# Revit family: Hager-UNIVERS-Hollow_wall-IP30-With_Cover-With_DIN-Hosted-DE-de
name_source: partatom
category: Electrical Equipment
units: mm (PartAtom-declared; Revit-internal decimal feet)

## family parameters
Cut with Voids When Loaded = No
Host = Face
Maintain Annotation Orientation = Yes
Panel Configuration = Two Columns, Circuits Across
Part Type = Panelboard
Room Calculation Point = No
Round Connector Dimension = Use Diameter
Shared = No

## types (28) — shared parameters
BC_MODEL_ID = 1539180
BC_OBJECT_ID = 512281
BC_OBJECT_VERSION = #6
Code hager = ADD-EC000214_EU
EF000003 - Montageart = Hohlwand
EF000007 - Farbe = weiß
EF000024 - UV-beständig = No
EF000049 - Tiefe = 125 mm  [stored 0.410105 ft]
EF000116 - RAL-Nummer = 9010
EF000118 - Mit Montageplatte = No
EF000218 - Einbautiefe = 112 mm  [stored 0.367454 ft]
EF001062 - EMV-Ausführung = No
EF001088 - Anbaumöglichkeit = Yes
EF001134 - DIN-Schiene = Yes
EF002950 - Breite in Teilungseinheiten = 12
EF004462 - Art der Schließung = sonstige
EF005474 - Schutzart (IP) = IP30
EF006244 - Transparenter Deckel/Tür = No
EF006306 - Mit Schloss = No
EF015941 - Signaldurchlassende Tür = No
ETIM class code = EC000214
ETIM class name = Small distribution board
HG000002-Mit tür = Yes
HG000003-Bereich = UNIVERS
HG000005-Dicke = 2 mm  [stored 0.00656168 ft]
HG000006-Flush mounted = Yes
HG000011-Leere Reihen von unten = No
HG000012-Türschwenkwinkel = 90.00°
HG000013-Tür links = No
HG000014-Tür rechts = Yes
HG000015-Sichtbarkeit der Türöffnung = Yes
HG000016-3D-Türsichtbarkeit = Yes
HG000017-Distanz zwischen den Polen = 18 mm  [stored 0.0590551 ft]
HG000060-RAL-number = 9010
HG000099-Onfly Template ID-de-DE = 507532
HGEF0002950-Breite in Teilungseinheiten = 12
Manufacturer = Hager
Name = Hager-UNIVERS-Hollow_wall-IP30-With_Cover-With_DIN-NoHosted-DE-de
Name BIM&CO = Electricity
Name hager = ADD_Enclosures_EC000214
Uniformat = Low Tension Service & Dist.
Uniformat code = D501001
zero-valued in all types: Default Elevation, EF001131 - Innentiefe, HG000007-Anzahl der leeren Spalten, HG000008-Anzahl der leeren Reihen

## per-type parameters (varying)
| type | BC_VARIANT_ID | EF000008 - Breite | EF000040 - Höhe | EF000266 - Anzahl der Reihen | EF000332 - Einbauhöhe | EF000846 - Einbaubreite | EF009212 - Ausführung Deckel | EF015776 - Erdungsklemmenblock | EF015777 - Neutralleiterklemmenblock | HG000001-Anzahl der Spalten | HG000004-Herstellerreferenz | HG000009-Doppelflügeligen Tür | HG000010-Asymmetrische Türen | HGEF000266-Anzahl der Reihen |
| UNIVERS-Hollow_wall_W353_H553_D125_12_Modular_Spacing-FWU31A | 1169890 | 353 mm  [stored 1.15814 ft] | 553 mm  [stored 1.8143 ft] | 3 | 502 mm  [stored 1.64698 ft] | 310 mm  [stored 1.01706 ft] | geschlossen | No | No | 1 | FWU31A | No | No | 3 |
| UNIVERS-Hollow_wall_W353_H553_D125_12_Modular_Spacing-FWU31S | 1169891 | 353 mm  [stored 1.15814 ft] | 553 mm  [stored 1.8143 ft] | 3 | 502 mm  [stored 1.64698 ft] | 310 mm  [stored 1.01706 ft] | mit Ausschnitt | Yes | Yes | 1 | FWU31S | No | No | 3 |
| UNIVERS-Hollow_wall_W603_H553_D125_12_Modular_Spacing-FWU32A | 1169892 | 603 mm | 553 mm  [stored 1.8143 ft] | 3 | 502 mm  [stored 1.64698 ft] | 560 mm  [stored 1.83727 ft] | geschlossen | No | No | 2 | FWU32A | No | No | 3 |
| UNIVERS-Hollow_wall_W603_H553_D125_12_Modular_Spacing-FWU32S | 1169893 | 603 mm | 553 mm  [stored 1.8143 ft] | 3 | 502 mm  [stored 1.64698 ft] | 560 mm  [stored 1.83727 ft] | mit Ausschnitt | Yes | No | 2 | FWU32S | No | No | 3 |
| UNIVERS-Hollow_wall_W853_H553_D125_12_Modular_Spacing-FWU33A | 1169894 | 853 mm  [stored 2.79856 ft] | 553 mm  [stored 1.8143 ft] | 3 | 502 mm  [stored 1.64698 ft] | 810 mm | geschlossen | No | No | 3 | FWU33A | Yes | Yes | 3 |
| UNIVERS-Hollow_wall_W853_H553_D125_12_Modular_Spacing-FWU33S | 1169895 | 853 mm  [stored 2.79856 ft] | 553 mm  [stored 1.8143 ft] | 3 | 502 mm  [stored 1.64698 ft] | 810 mm | mit Ausschnitt | Yes | No | 3 | FWU33S | Yes | Yes | 3 |
| UNIVERS-Hollow_wall_W353_H703_D125_12_Modular_Spacing-FWU41A | 1169896 | 353 mm  [stored 1.15814 ft] | 703 mm  [stored 2.30643 ft] | 4 | 652 mm  [stored 2.13911 ft] | 310 mm  [stored 1.01706 ft] | geschlossen | No | No | 1 | FWU41A | No | No | 4 |
| UNIVERS-Hollow_wall_W353_H703_D125_12_Modular_Spacing-FWU41S | 1169897 | 353 mm  [stored 1.15814 ft] | 703 mm  [stored 2.30643 ft] | 4 | 652 mm  [stored 2.13911 ft] | 310 mm  [stored 1.01706 ft] | mit Ausschnitt | Yes | No | 1 | FWU41S | No | No | 4 |
| UNIVERS-Hollow_wall_W603_H703_D125_12_Modular_Spacing-FWU42A | 1169898 | 603 mm | 703 mm  [stored 2.30643 ft] | 4 | 652 mm  [stored 2.13911 ft] | 560 mm  [stored 1.83727 ft] | geschlossen | No | No | 2 | FWU42A | No | No | 4 |
| UNIVERS-Hollow_wall_W603_H703_D125_12_Modular_Spacing-FWU42S | 1169899 | 603 mm | 703 mm  [stored 2.30643 ft] | 4 | 652 mm  [stored 2.13911 ft] | 560 mm  [stored 1.83727 ft] | mit Ausschnitt | Yes | No | 2 | FWU42S | No | No | 4 |
| UNIVERS-Hollow_wall_W853_H703_D125_12_Modular_Spacing-FWU43A | 1169900 | 853 mm  [stored 2.79856 ft] | 703 mm  [stored 2.30643 ft] | 4 | 652 mm  [stored 2.13911 ft] | 810 mm | geschlossen | No | No | 3 | FWU43A | Yes | Yes | 4 |
| UNIVERS-Hollow_wall_W853_H703_D125_12_Modular_Spacing-FWU43S | 1169901 | 853 mm  [stored 2.79856 ft] | 703 mm  [stored 2.30643 ft] | 4 | 652 mm  [stored 2.13911 ft] | 810 mm | mit Ausschnitt | Yes | No | 3 | FWU43S | Yes | Yes | 4 |
| UNIVERS-Hollow_wall_W353_H853_D125_12_Modular_Spacing-FWU51A | 1169902 | 353 mm  [stored 1.15814 ft] | 853 mm  [stored 2.79856 ft] | 5 | 802 mm  [stored 2.63123 ft] | 310 mm  [stored 1.01706 ft] | geschlossen | No | No | 1 | FWU51A | No | No | 5 |
| UNIVERS-Hollow_wall_W353_H853_D125_12_Modular_Spacing-FWU51S | 1169903 | 353 mm  [stored 1.15814 ft] | 853 mm  [stored 2.79856 ft] | 5 | 802 mm  [stored 2.63123 ft] | 310 mm  [stored 1.01706 ft] | mit Ausschnitt | Yes | No | 1 | FWU51S | No | No | 5 |
| UNIVERS-Hollow_wall_W603_H853_D125_12_Modular_Spacing-FWU52A | 1169904 | 603 mm | 853 mm  [stored 2.79856 ft] | 5 | 802 mm  [stored 2.63123 ft] | 560 mm  [stored 1.83727 ft] | geschlossen | No | No | 2 | FWU52A | No | No | 5 |
| UNIVERS-Hollow_wall_W603_H853_D125_12_Modular_Spacing-FWU52S | 1169905 | 603 mm | 853 mm  [stored 2.79856 ft] | 5 | 802 mm  [stored 2.63123 ft] | 560 mm  [stored 1.83727 ft] | mit Ausschnitt | Yes | No | 2 | FWU52S | No | No | 5 |
| UNIVERS-Hollow_wall_W353_H1003_D125_12_Modular_Spacing-FWU61A | 1169906 | 353 mm  [stored 1.15814 ft] | 1003 mm  [stored 3.29068 ft] | 6 | 952 mm  [stored 3.12336 ft] | 310 mm  [stored 1.01706 ft] | geschlossen | No | No | 1 | FWU61A | No | No | 6 |
| UNIVERS-Hollow_wall_W353_H1003_D125_12_Modular_Spacing-FWU61S | 1169907 | 353 mm  [stored 1.15814 ft] | 1003 mm  [stored 3.29068 ft] | 6 | 952 mm  [stored 3.12336 ft] | 310 mm  [stored 1.01706 ft] | mit Ausschnitt | Yes | No | 1 | FWU61S | No | No | 6 |
| UNIVERS-Hollow_wall_W603_H1003_D125_12_Modular_Spacing-FWU62A | 1169908 | 603 mm | 1003 mm  [stored 3.29068 ft] | 6 | 952 mm  [stored 3.12336 ft] | 560 mm  [stored 1.83727 ft] | geschlossen | No | No | 2 | FWU62A | No | No | 6 |
| UNIVERS-Hollow_wall_W603_H1003_D125_12_Modular_Spacing-FWU62S | 1169909 | 603 mm | 1003 mm  [stored 3.29068 ft] | 6 | 952 mm  [stored 3.12336 ft] | 560 mm  [stored 1.83727 ft] | mit Ausschnitt | Yes | No | 2 | FWU62S | No | No | 6 |
| UNIVERS-Hollow_wall_W853_H1003_D125_12_Modular_Spacing-FWU63A | 1169910 | 853 mm  [stored 2.79856 ft] | 1003 mm  [stored 3.29068 ft] | 6 | 952 mm  [stored 3.12336 ft] | 810 mm | geschlossen | No | No | 3 | FWU63A | Yes | Yes | 6 |
| UNIVERS-Hollow_wall_W853_H1003_D125_12_Modular_Spacing-FWU63S | 1169911 | 853 mm  [stored 2.79856 ft] | 1003 mm  [stored 3.29068 ft] | 6 | 952 mm  [stored 3.12336 ft] | 810 mm | mit Ausschnitt | Yes | No | 3 | FWU63S | Yes | Yes | 6 |
| UNIVERS-Hollow_wall_W353_H1153_D125_12_Modular_Spacing-FWU71A | 1169912 | 353 mm  [stored 1.15814 ft] | 1153 mm | 7 | 1102 mm  [stored 3.61549 ft] | 310 mm  [stored 1.01706 ft] | geschlossen | No | No | 1 | FWU71A | No | No | 7 |
| UNIVERS-Hollow_wall_W353_H1153_D125_12_Modular_Spacing-FWU71S | 1169913 | 353 mm  [stored 1.15814 ft] | 1153 mm | 7 | 1102 mm  [stored 3.61549 ft] | 310 mm  [stored 1.01706 ft] | mit Ausschnitt | Yes | No | 1 | FWU71S | No | No | 7 |
| UNIVERS-Hollow_wall_W603_H1153_D125_12_Modular_Spacing-FWU72A | 1169914 | 603 mm | 1153 mm | 7 | 1102 mm  [stored 3.61549 ft] | 560 mm  [stored 1.83727 ft] | geschlossen | No | No | 2 | FWU72A | No | No | 7 |
| UNIVERS-Hollow_wall_W603_H1153_D125_12_Modular_Spacing-FWU72S | 1169915 | 603 mm | 1153 mm | 7 | 1102 mm  [stored 3.61549 ft] | 560 mm  [stored 1.83727 ft] | mit Ausschnitt | Yes | No | 2 | FWU72S | No | No | 7 |
| UNIVERS-Hollow_wall_W853_H1153_D125_12_Modular_Spacing-FWU73A | 1169916 | 853 mm  [stored 2.79856 ft] | 1153 mm | 7 | 1102 mm  [stored 3.61549 ft] | 810 mm | geschlossen | No | No | 3 | FWU73A | Yes | Yes | 7 |
| UNIVERS-Hollow_wall_W853_H1153_D125_12_Modular_Spacing-FWU73S | 1169917 | 853 mm  [stored 2.79856 ft] | 1153 mm | 7 | 1102 mm  [stored 3.61549 ft] | 810 mm | mit Ausschnitt | Yes | Yes | 3 | FWU73S | Yes | Yes | 7 |

note: column(s) folded — value = type name in every type: Reference

note: [stored X ft] marks values corroborated as IEEE doubles in the binary element streams (Revit-internal decimal feet)

## geometry (parser evidence)
native form markers: Sweep x17
no freeform markers — native parametric forms only
